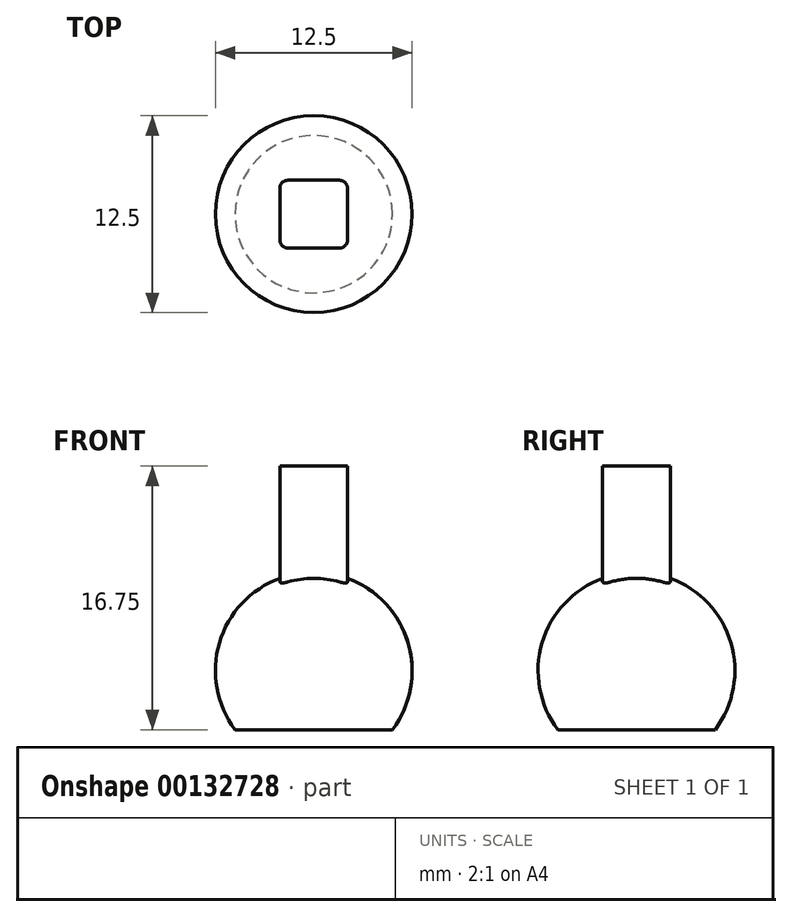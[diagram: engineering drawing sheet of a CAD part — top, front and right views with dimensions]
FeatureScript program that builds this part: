
annotation { "Feature Type Name" : "Feature", "Feature Type Description" : "" }
export const myFeature = defineFeature(function(context is Context, id is Id, definition is map)
    precondition{}
    {
        {
            var Q0;
            Q0=qCreatedBy(makeId("Front.planeOp"),FACE);
            var sketch = newSketch(context, id + "F0", { "sketchPlane" : qUnion([Q0])});
            skArc(sketch, "E0", {"start": v(0, 6.25) * mm, "mid": v(-5.6, 2.8) * mm, "end": v(-5, -3.75) * mm});
            skLineSegment(sketch, "E1", {"start": v(0, 6.25) * mm, "end": v(0, -3.75) * mm});
            skLineSegment(sketch, "E2.bottom", {"start": v(-2.15, 0) * mm, "end": v(2.15, 0) * mm});
            skLineSegment(sketch, "E2.top", {"start": v(-2.15, 13) * mm, "end": v(2.15, 13) * mm});
            skLineSegment(sketch, "E2.left", {"start": v(-2.15, 0) * mm, "end": v(-2.15, 13) * mm});
            skLineSegment(sketch, "E2.right", {"start": v(2.15, 0) * mm, "end": v(2.15, 13) * mm});
            skLineSegment(sketch, "E3", {"start": v(0, -3.75) * mm, "end": v(-5, -3.75) * mm});
            skPoint(sketch, "E4.orphan", {"position": v(0, -6.25) * mm});
            skSolve(sketch);
        }
        {
            var Q0;
            {var subQ7=sQuery(id+"F0.wireOp",EDGE,"E3");Q0=makeQuery(id+"F0.imprint","IMPRINT",FACE,{"disambiguationData":[TD([[makeQuery(id+"F0.imprint","IMPRINT",EDGE,{"derivedFrom":subQ7}),-1.0]])]});}
            var Q1;
            {var subQ0=sQuery(id+"F0.wireOp",EDGE,"E1");var subQ1=sQuery(id+"F0.wireOp",EDGE,"E0");var subQ2=makeQuery(id+"F0.imprint","INTERSECT",VERTEX,{"derivedFrom":[subQ1,subQ0]});Q1=makeQuery(id+"F0.imprint","IMPRINT",FACE,{"disambiguationData":[TD([[makeQuery(id+"F0.imprint","IMPRINT",EDGE,{"disambiguationData":[TD([[subQ2,-1.0]])],"derivedFrom":subQ1}),1.0]])]});}
            var Q2;
            Q2=sQuery(id+"F0.wireOp",EDGE,"E1");
            revolve(context, id + "F1", {"entities" : qUnion([Q0, Q1]), "axis" : qUnion([Q2]), "revolveType" : RevolveType.FULL});
        }
        {
            var Q0;
            {var subQ0=sQuery(id+"F0.wireOp",EDGE,"E1");var subQ1=sQuery(id+"F0.wireOp",EDGE,"E0");var subQ2=makeQuery(id+"F0.imprint","INTERSECT",VERTEX,{"derivedFrom":[subQ1,subQ0]});Q0=makeQuery(id+"F0.imprint","IMPRINT",FACE,{"disambiguationData":[TD([[makeQuery(id+"F0.imprint","IMPRINT",EDGE,{"disambiguationData":[TD([[subQ2,-1.0]])],"derivedFrom":subQ1}),1.0]])]});}
            var Q1;
            {var subQ0=sQuery(id+"F0.wireOp",EDGE,"E2.top");Q1=makeQuery(id+"F0.imprint","IMPRINT",FACE,{"disambiguationData":[TD([[makeQuery(id+"F0.imprint","IMPRINT",EDGE,{"derivedFrom":subQ0}),-1.0]])]});}
            extrude(context, id + "F2", {"entities" : qUnion([Q0, Q1]), "operationType" : NewBodyOperationType.ADD, "endBound" : BoundingType.SYMMETRIC, "depth" : 4.3 * mm});
        }
        {
            var Q0;
            Q0=makeQuery(id+"F2.opExtrude","CAP_EDGE",EDGE,{"disambiguationData":[OSD([sQuery(id+"F0.wireOp",EDGE,"E2.left")])],"isStart":false});
            var Q1;
            Q1=makeQuery(id+"F2.opExtrude","CAP_EDGE",EDGE,{"disambiguationData":[OSD([sQuery(id+"F0.wireOp",EDGE,"E2.left")])],"isStart":true});
            var Q2;
            Q2=makeQuery(id+"F2.opExtrude","CAP_EDGE",EDGE,{"disambiguationData":[OSD([sQuery(id+"F0.wireOp",EDGE,"E2.right")])],"isStart":false});
            var Q3;
            Q3=makeQuery(id+"F2.opExtrude","CAP_EDGE",EDGE,{"disambiguationData":[OSD([sQuery(id+"F0.wireOp",EDGE,"E2.right")])],"isStart":true});
            fillet(context, id + "F3", {"entities" : qUnion([Q0, Q1, Q2, Q3]), "radius" : 0.5 * mm, "allowEdgeOverflow" : false});
        }
    });
